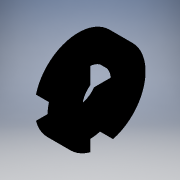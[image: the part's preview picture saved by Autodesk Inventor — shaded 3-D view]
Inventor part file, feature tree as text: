
AUTODESK INVENTOR PART (.ipt)
format: ipt  version: 2017.3 (Build 213256000, 256)  size: 110,080 bytes
history: native  units: mm (DEFAULTED — no unit token found)
features: other x7, sketch x3, extrude x2, revolve x1
ambient origin geometry x8: Origin, YZ Plane, XZ Plane, XY Plane, X Axis, Y Axis, Z Axis, Center Point
bodies: Solid1 (feature_tree)
feature tree (13):
  revolve  "Revolution1"  [1 undecoded]
  extrude  "Extrusion1"  [1 undecoded]
  extrude  "Extrusion2"  [1 undecoded]
  other  "C_XY"
  other  "C_YZ"
  other  "C_ZX"
  other  "C_X"
  other  "C_Y"
  other  "C_Z"
  other  "C_Center"
  sketch  "Sketch_1"  dims[d0=360.0deg d1=27.0mm d2=0.0mm]
  sketch  "Sketch_2"  dims[d3=27.0mm d4=0.0mm]
  sketch  "Sketch_3"
note: 3 required parameter values undecoded (feature->parameter linkage not recoverable at this tier; creation-order binding heuristic only, values carry confidence <= 0.55)